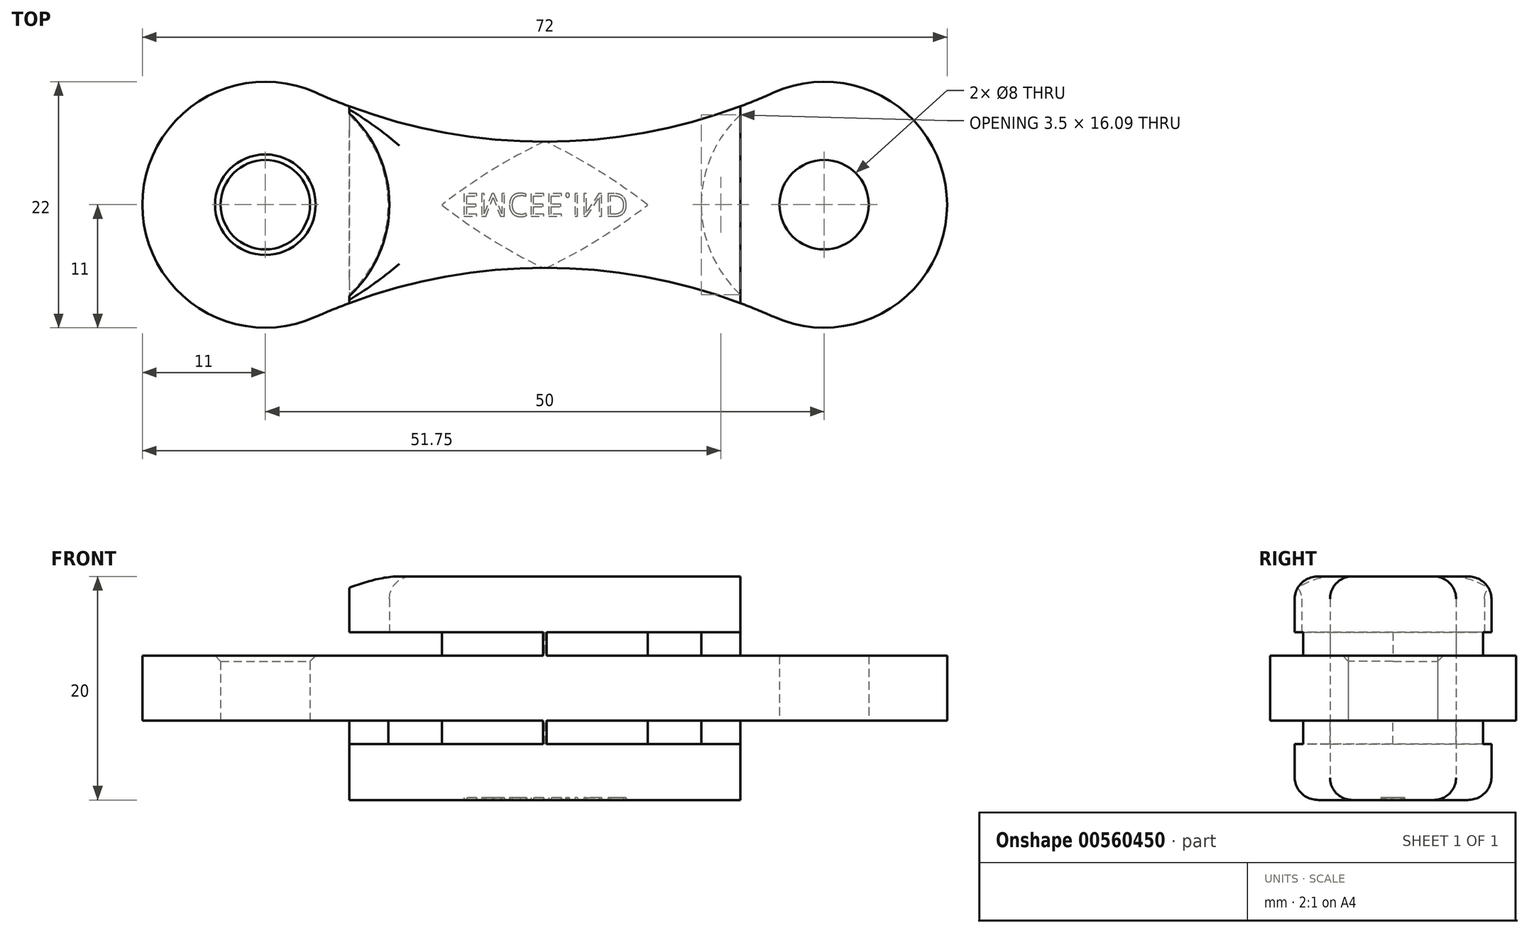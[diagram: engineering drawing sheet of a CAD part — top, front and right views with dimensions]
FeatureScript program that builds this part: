
annotation { "Feature Type Name" : "Feature", "Feature Type Description" : "" }
export const myFeature = defineFeature(function(context is Context, id is Id, definition is map)
    precondition{}
    {
        {
            var Q0;
            Q0=qCreatedBy(makeId("Top.planeOp"),FACE);
            var sketch = newSketch(context, id + "F0", { "sketchPlane" : qUnion([Q0])});
            skArc(sketch, "E0", {"start": v(-20.5, 10.03) * mm, "mid": v(-36, 0) * mm, "end": v(-20.5, -10.03) * mm});
            skArc(sketch, "E1", {"start": v(20.5, -10.03) * mm, "mid": v(36, 0) * mm, "end": v(20.5, 10.03) * mm});
            skArc(sketch, "E2", {"start": v(-20.5, 10.03) * mm, "mid": v(0, 5.64) * mm, "end": v(20.5, 10.03) * mm});
            skLineSegment(sketch, "E3", {"start": v(-25, 0) * mm, "end": v(25, 0) * mm, "construction": true});
            skArc(sketch, "E4.MirrorC", {"start": v(-20.5, -10.03) * mm, "mid": v(0, -5.64) * mm, "end": v(20.5, -10.03) * mm});
            skSolve(sketch);
        }
        {
            var Q0;
            Q0=makeQuery(id+"F0.imprint","IMPRINT",FACE,{"disambiguationData":[TD([[makeQuery(id+"F0.imprint","IMPRINT",EDGE,{"derivedFrom":sQuery(id+"F0.wireOp",EDGE,"E0")}),1.0]])]});
            extrude(context, id + "F1", {"entities" : qUnion([Q0]), "endBound" : BoundingType.SYMMETRIC, "depth" : 20 * mm, "offsetDistance" : 25 * mm});
        }
        {
            var Q0;
            Q0=qCreatedBy(makeId("Front.planeOp"),FACE);
            var sketch = newSketch(context, id + "F2", { "sketchPlane" : qUnion([Q0])});
            skLineSegment(sketch, "E5.bottom", {"start": v(-17.5, -15) * mm, "end": v(-52.5, -15) * mm});
            skLineSegment(sketch, "E5.top", {"start": v(-17.5, -2.9) * mm, "end": v(-52.5, -2.9) * mm});
            skLineSegment(sketch, "E5.left", {"start": v(-17.5, -15) * mm, "end": v(-17.5, -2.9) * mm});
            skLineSegment(sketch, "E5.right", {"start": v(-52.5, -15) * mm, "end": v(-52.5, -2.9) * mm});
            skPoint(sketch, "E5.middle", {"position": v(-35, -8.95) * mm});
            skLineSegment(sketch, "E6", {"start": v(0, 15.36) * mm, "end": v(0, 51.66) * mm, "construction": true});
            skLineSegment(sketch, "E7.MirrorCS", {"start": v(17.5, -15) * mm, "end": v(17.5, -2.9) * mm});
            skLineSegment(sketch, "E8.MirrorCS", {"start": v(17.5, -15) * mm, "end": v(52.5, -15) * mm});
            skLineSegment(sketch, "E9.MirrorCS", {"start": v(17.5, -2.9) * mm, "end": v(52.5, -2.9) * mm});
            skLineSegment(sketch, "E10.MirrorCS", {"start": v(52.5, -15) * mm, "end": v(52.5, -2.9) * mm});
            skLineSegment(sketch, "E11", {"start": v(0, 0) * mm, "end": v(62.43, 0) * mm, "construction": true});
            skLineSegment(sketch, "E12.MirrorCS", {"start": v(-17.5, 2.9) * mm, "end": v(-52.5, 2.9) * mm});
            skLineSegment(sketch, "E13.MirrorCS", {"start": v(-52.5, 15) * mm, "end": v(-52.5, 2.9) * mm});
            skLineSegment(sketch, "E14.MirrorCS", {"start": v(-17.5, 15) * mm, "end": v(-52.5, 15) * mm});
            skLineSegment(sketch, "E15.MirrorCS", {"start": v(-17.5, 15) * mm, "end": v(-17.5, 2.9) * mm});
            skLineSegment(sketch, "E16.MirrorCS", {"start": v(17.5, 15) * mm, "end": v(17.5, 2.9) * mm});
            skLineSegment(sketch, "E17.MirrorCS", {"start": v(17.5, 2.9) * mm, "end": v(52.5, 2.9) * mm});
            skLineSegment(sketch, "E18.MirrorCS", {"start": v(17.5, 15) * mm, "end": v(52.5, 15) * mm});
            skLineSegment(sketch, "E19.MirrorCS", {"start": v(52.5, 15) * mm, "end": v(52.5, 2.9) * mm});
            skSolve(sketch);
        }
        {
            var Q0;
            Q0=makeQuery(id+"F2.imprint","IMPRINT",FACE,{"disambiguationData":[TD([[makeQuery(id+"F2.imprint","IMPRINT",EDGE,{"derivedFrom":sQuery(id+"F2.wireOp",EDGE,"E12.MirrorCS")}),-1.0]])]});
            var Q1;
            Q1=makeQuery(id+"F2.imprint","IMPRINT",FACE,{"disambiguationData":[TD([[makeQuery(id+"F2.imprint","IMPRINT",EDGE,{"derivedFrom":sQuery(id+"F2.wireOp",EDGE,"E5.bottom")}),-1.0]])]});
            var Q2;
            Q2=makeQuery(id+"F2.imprint","IMPRINT",FACE,{"disambiguationData":[TD([[makeQuery(id+"F2.imprint","IMPRINT",EDGE,{"derivedFrom":sQuery(id+"F2.wireOp",EDGE,"E16.MirrorCS")}),1.0]])]});
            var Q3;
            Q3=makeQuery(id+"F2.imprint","IMPRINT",FACE,{"disambiguationData":[TD([[makeQuery(id+"F2.imprint","IMPRINT",EDGE,{"derivedFrom":sQuery(id+"F2.wireOp",EDGE,"E7.MirrorCS")}),-1.0]])]});
            extrude(context, id + "F3", {"entities" : qUnion([Q0, Q1, Q2, Q3]), "operationType" : NewBodyOperationType.REMOVE, "endBound" : BoundingType.SYMMETRIC, "oppositeDirection" : true, "depth" : 25 * mm, "offsetDistance" : 25 * mm});
        }
        {
            var Q0;
            Q0=makeQuery(id+"F3.boolean.opBoolean","COPY",FACE,{"derivedFrom":makeQuery(id+"F3.opExtrude","SWEPT_FACE",FACE,{"disambiguationData":[OSD([sQuery(id+"F2.wireOp",EDGE,"E12.MirrorCS")])]})});
            var sketch = newSketch(context, id + "F4", { "sketchPlane" : qUnion([Q0])});
            skCircle(sketch, "E20", {"center": v(-25, 0) * mm, "radius": 11.1 * mm});
            skLineSegment(sketch, "E21", {"start": v(0, -2.73) * mm, "end": v(0, 23.97) * mm, "construction": true});
            skCircle(sketch, "E22.MirrorC", {"center": v(25, 0) * mm, "radius": 11.1 * mm});
            skLineSegment(sketch, "E23", {"start": v(0, -6.47) * mm, "end": v(-9.77, -6.47) * mm});
            skSolve(sketch);
        }
        {
            var Q0;
            {var subQ0=sQuery(id+"F4.wireOp",EDGE,"E20");var subQ1=makeQuery(id+"F3.boolean.opBoolean","COPY",EDGE,{"derivedFrom":makeQuery(id+"F3.opExtrude","SWEPT_EDGE",EDGE,{"disambiguationData":[OSD([sQuery(id+"F2.wireOp",EDGE,"E12.MirrorCS"),sQuery(id+"F2.wireOp",EDGE,"E15.MirrorCS")])]})});var subQ2=makeQuery(id+"F4.imprint","INTERSECT",VERTEX,{"disambiguationData":[OD(0.0)],"derivedFrom":[subQ1,subQ0]});Q0=makeQuery(id+"F4.imprint","IMPRINT",FACE,{"disambiguationData":[TD([[makeQuery(id+"F4.imprint","IMPRINT",EDGE,{"disambiguationData":[TD([[subQ2,1.0]])],"derivedFrom":subQ0}),1.0]])]});}
            var Q1;
            {var subQ1=sQuery(id+"F2.wireOp",EDGE,"E12.MirrorCS");var subQ5=makeQuery(id+"F3.opExtrude","SWEPT_FACE",FACE,{"disambiguationData":[OSD([subQ1])]});var subQ8=makeQuery(id+"F3.boolean.opBoolean","INTERSECT",EDGE,{"derivedFrom":[makeQuery(id+"F1.opExtrude","SWEPT_FACE",FACE,{"disambiguationData":[OSD([sQuery(id+"F0.wireOp",EDGE,"E0")])]}),subQ5]});Q1=makeQuery(id+"F4.imprint","IMPRINT",FACE,{"disambiguationData":[TD([[makeQuery(id+"F4.imprint","IMPRINT",EDGE,{"derivedFrom":subQ8}),1.0]])]});}
            var Q2;
            Q2=makeQuery(id+"F4.imprint","IMPRINT",FACE,{"disambiguationData":[TD([[makeQuery(id+"F4.imprint","IMPRINT",EDGE,{"derivedFrom":sQuery(id+"F4.wireOp",EDGE,"E22.MirrorC")}),-1.0]])]});
            extrude(context, id + "F5", {"entities" : qUnion([Q0, Q1, Q2]), "operationType" : NewBodyOperationType.REMOVE, "depth" : 10 * mm, "offsetDistance" : 25 * mm});
        }
        {
            var Q0;
            Q0=makeQuery(id+"F3.boolean.opBoolean","COPY",FACE,{"derivedFrom":makeQuery(id+"F3.opExtrude","SWEPT_FACE",FACE,{"disambiguationData":[OSD([sQuery(id+"F2.wireOp",EDGE,"E5.top")])]})});
            var sketch = newSketch(context, id + "F6", { "sketchPlane" : qUnion([Q0])});
            skCircle(sketch, "E24", {"center": v(-25, 0) * mm, "radius": 11.1 * mm});
            skLineSegment(sketch, "E25", {"start": v(0, -7.37) * mm, "end": v(0, 19.33) * mm, "construction": true});
            skCircle(sketch, "E26.MirrorC", {"center": v(25, 0) * mm, "radius": 11.1 * mm});
            skSolve(sketch);
        }
        {
            var Q0;
            Q0=makeQuery(id+"F6.imprint","IMPRINT",FACE,{"disambiguationData":[TD([[makeQuery(id+"F6.imprint","IMPRINT",EDGE,{"derivedFrom":sQuery(id+"F6.wireOp",EDGE,"E26.MirrorC")}),-1.0]])]});
            var Q1;
            {var subQ1=sQuery(id+"F2.wireOp",EDGE,"E5.top");var subQ5=makeQuery(id+"F3.opExtrude","SWEPT_FACE",FACE,{"disambiguationData":[OSD([subQ1])]});var subQ8=makeQuery(id+"F3.boolean.opBoolean","INTERSECT",EDGE,{"derivedFrom":[makeQuery(id+"F1.opExtrude","SWEPT_FACE",FACE,{"disambiguationData":[OSD([sQuery(id+"F0.wireOp",EDGE,"E0")])]}),subQ5]});Q1=makeQuery(id+"F6.imprint","IMPRINT",FACE,{"disambiguationData":[TD([[makeQuery(id+"F6.imprint","IMPRINT",EDGE,{"derivedFrom":subQ8}),-1.0]])]});}
            var Q2;
            {var subQ0=sQuery(id+"F6.wireOp",EDGE,"E24");var subQ1=makeQuery(id+"F3.boolean.opBoolean","COPY",EDGE,{"derivedFrom":makeQuery(id+"F3.opExtrude","SWEPT_EDGE",EDGE,{"disambiguationData":[OSD([sQuery(id+"F2.wireOp",EDGE,"E5.top"),sQuery(id+"F2.wireOp",EDGE,"E5.left")])]})});var subQ2=makeQuery(id+"F6.imprint","INTERSECT",VERTEX,{"disambiguationData":[OD(0.0)],"derivedFrom":[subQ1,subQ0]});Q2=makeQuery(id+"F6.imprint","IMPRINT",FACE,{"disambiguationData":[TD([[makeQuery(id+"F6.imprint","IMPRINT",EDGE,{"disambiguationData":[TD([[subQ2,1.0]])],"derivedFrom":subQ0}),1.0]])]});}
            extrude(context, id + "F7", {"entities" : qUnion([Q0, Q1, Q2]), "operationType" : NewBodyOperationType.REMOVE, "depth" : 10 * mm, "offsetDistance" : 25 * mm});
        }
        {
            var Q0;
            Q0=qCreatedBy(makeId("Front.planeOp"),FACE);
            var sketch = newSketch(context, id + "F8", { "sketchPlane" : qUnion([Q0])});
            skLineSegment(sketch, "E27.bottom", {"start": v(2, 5) * mm, "end": v(-10, 5) * mm});
            skLineSegment(sketch, "E27.top", {"start": v(2, -5) * mm, "end": v(-10, -5) * mm});
            skLineSegment(sketch, "E27.left", {"start": v(5, 2) * mm, "end": v(5, -2) * mm});
            skLineSegment(sketch, "E27.right", {"start": v(-13, 2) * mm, "end": v(-13, -2) * mm});
            skPoint(sketch, "E27.middle", {"position": v(-2, 0) * mm});
            skPoint(sketch, "E28.visualSharp", {"position": v(-13, 5) * mm});
            skArc(sketch, "E28.filletArc", {"start": v(-10, 5) * mm, "mid": v(-12.12, 4.12) * mm, "end": v(-13, 2) * mm});
            skPoint(sketch, "E29.visualSharp", {"position": v(-13, -5) * mm});
            skArc(sketch, "E29.filletArc", {"start": v(-13, -2) * mm, "mid": v(-12.12, -4.12) * mm, "end": v(-10, -5) * mm});
            skPoint(sketch, "E30.visualSharp", {"position": v(5, -5) * mm});
            skArc(sketch, "E30.filletArc", {"start": v(2, -5) * mm, "mid": v(4.12, -4.12) * mm, "end": v(5, -2) * mm});
            skPoint(sketch, "E31.visualSharp", {"position": v(5, 5) * mm});
            skArc(sketch, "E31.filletArc", {"start": v(5, 2) * mm, "mid": v(4.12, 4.12) * mm, "end": v(2, 5) * mm});
            skSolve(sketch);
        }
        {
            var Q0;
            Q0=makeQuery(id+"F7.boolean.opBoolean","INTERSECT",EDGE,{"derivedFrom":[makeQuery(id+"F1.opExtrude","CAP_FACE",FACE,{"disambiguationData":[OSD([sQuery(id+"F0.wireOp",EDGE,"E0"),sQuery(id+"F0.wireOp",EDGE,"E1"),sQuery(id+"F0.wireOp",EDGE,"E2"),sQuery(id+"F0.wireOp",EDGE,"E4.MirrorC")])],"isStart":true}),makeQuery(id+"F7.opExtrude","SWEPT_FACE",FACE,{"disambiguationData":[OSD([sQuery(id+"F6.wireOp",EDGE,"E24")])]})]});
            var Q1;
            Q1=makeQuery(id+"F7.boolean.opBoolean","INTERSECT",EDGE,{"derivedFrom":[makeQuery(id+"F1.opExtrude","CAP_FACE",FACE,{"disambiguationData":[OSD([sQuery(id+"F0.wireOp",EDGE,"E0"),sQuery(id+"F0.wireOp",EDGE,"E1"),sQuery(id+"F0.wireOp",EDGE,"E2"),sQuery(id+"F0.wireOp",EDGE,"E4.MirrorC")])],"isStart":true}),makeQuery(id+"F7.opExtrude","SWEPT_FACE",FACE,{"disambiguationData":[OSD([sQuery(id+"F6.wireOp",EDGE,"E26.MirrorC")])]})]});
            var Q2;
            Q2=makeQuery(id+"F1.opExtrude","CAP_EDGE",EDGE,{"disambiguationData":[OSD([sQuery(id+"F0.wireOp",EDGE,"E2")])],"isStart":true});
            var Q3;
            Q3=makeQuery(id+"F1.opExtrude","CAP_EDGE",EDGE,{"disambiguationData":[OSD([sQuery(id+"F0.wireOp",EDGE,"E4.MirrorC")])],"isStart":true});
            var Q4;
            Q4=makeQuery(id+"F5.boolean.opBoolean","INTERSECT",EDGE,{"derivedFrom":[makeQuery(id+"F1.opExtrude","CAP_FACE",FACE,{"disambiguationData":[OSD([sQuery(id+"F0.wireOp",EDGE,"E0"),sQuery(id+"F0.wireOp",EDGE,"E1"),sQuery(id+"F0.wireOp",EDGE,"E2"),sQuery(id+"F0.wireOp",EDGE,"E4.MirrorC")])],"isStart":false}),makeQuery(id+"F5.opExtrude","SWEPT_FACE",FACE,{"disambiguationData":[OSD([sQuery(id+"F4.wireOp",EDGE,"E20")])]})]});
            var Q5;
            Q5=makeQuery(id+"F5.boolean.opBoolean","INTERSECT",EDGE,{"derivedFrom":[makeQuery(id+"F1.opExtrude","CAP_FACE",FACE,{"disambiguationData":[OSD([sQuery(id+"F0.wireOp",EDGE,"E0"),sQuery(id+"F0.wireOp",EDGE,"E1"),sQuery(id+"F0.wireOp",EDGE,"E2"),sQuery(id+"F0.wireOp",EDGE,"E4.MirrorC")])],"isStart":false}),makeQuery(id+"F5.opExtrude","SWEPT_FACE",FACE,{"disambiguationData":[OSD([sQuery(id+"F4.wireOp",EDGE,"E22.MirrorC")])]})]});
            var Q6;
            Q6=makeQuery(id+"F1.opExtrude","CAP_EDGE",EDGE,{"disambiguationData":[OSD([sQuery(id+"F0.wireOp",EDGE,"E2")])],"isStart":false});
            var Q7;
            Q7=makeQuery(id+"F1.opExtrude","CAP_EDGE",EDGE,{"disambiguationData":[OSD([sQuery(id+"F0.wireOp",EDGE,"E4.MirrorC")])],"isStart":false});
            fillet(context, id + "F9", {"entities" : qUnion([Q0, Q1, Q2, Q3, Q4, Q5, Q6, Q7]), "radius" : 2 * mm, "tangentPropagation" : true, "allowEdgeOverflow" : false});
        }
        {
            var Q0;
            {var subQ1=sQuery(id+"F2.wireOp",EDGE,"E5.top");var subQ5=makeQuery(id+"F3.opExtrude","SWEPT_FACE",FACE,{"disambiguationData":[OSD([subQ1])]});var subQ8=makeQuery(id+"F3.boolean.opBoolean","INTERSECT",EDGE,{"derivedFrom":[makeQuery(id+"F1.opExtrude","SWEPT_FACE",FACE,{"disambiguationData":[OSD([sQuery(id+"F0.wireOp",EDGE,"E0")])]}),subQ5]});Q0=makeQuery(id+"F6.imprint","IMPRINT",FACE,{"disambiguationData":[TD([[makeQuery(id+"F6.imprint","IMPRINT",EDGE,{"derivedFrom":subQ8}),-1.0]])]});}
            var sketch = newSketch(context, id + "F10", { "sketchPlane" : qUnion([Q0])});
            skCircle(sketch, "E32", {"center": v(-25, 0) * mm, "radius": 4 * mm});
            skCircle(sketch, "E33", {"center": v(25, 0) * mm, "radius": 4 * mm});
            skSolve(sketch);
        }
        {
            var Q0;
            Q0 = qSketchRegion(id + "F10", true);
            extrude(context, id + "F11", {"entities" : qUnion([Q0]), "operationType" : NewBodyOperationType.REMOVE, "endBound" : BoundingType.THROUGH_ALL, "oppositeDirection" : true, "depth" : 25 * mm, "offsetDistance" : 25 * mm});
        }
        {
            var Q0;
            {var subQ0=sQuery(id+"F2.wireOp",EDGE,"E12.MirrorCS");Q0=makeQuery(id+"F5.boolean.opBoolean","MERGE",FACE,{"derivedFrom":[makeQuery(id+"F3.boolean.opBoolean","COPY",FACE,{"derivedFrom":makeQuery(id+"F3.opExtrude","SWEPT_FACE",FACE,{"disambiguationData":[OSD([subQ0])]})}),makeQuery(id+"F5.opExtrude","CAP_FACE",FACE,{"disambiguationData":[OSD([sQuery(id+"F0.wireOp",EDGE,"E0"),sQuery(id+"F0.wireOp",EDGE,"E2"),sQuery(id+"F0.wireOp",EDGE,"E4.MirrorC"),subQ0,sQuery(id+"F4.wireOp",EDGE,"E20")])],"isStart":true})]});}
            var sketch = newSketch(context, id + "F12", { "sketchPlane" : qUnion([Q0])});
            skArc(sketch, "E34", {"start": v(-13.16, 16.12) * mm, "mid": v(-45, 0) * mm, "end": v(-13.16, -16.12) * mm});
            skLineSegment(sketch, "E35", {"start": v(0, -6.46) * mm, "end": v(-13.16, -16.12) * mm});
            skLineSegment(sketch, "E36", {"start": v(0, 6.46) * mm, "end": v(-13.16, 16.12) * mm});
            skLineSegment(sketch, "E37.MirrorCS", {"start": v(0, -6.46) * mm, "end": v(13.16, -16.12) * mm});
            skLineSegment(sketch, "E38.MirrorCS", {"start": v(0, 6.46) * mm, "end": v(13.16, 16.12) * mm});
            skArc(sketch, "E39.MirrorCS", {"start": v(13.16, 16.12) * mm, "mid": v(45, 0) * mm, "end": v(13.16, -16.12) * mm});
            skArc(sketch, "E40", {"start": v(-9.2, -0.01) * mm, "mid": v(-4.76, -3.12) * mm, "end": v(0, -5.72) * mm});
            skArc(sketch, "E41", {"start": v(9.2, -0.01) * mm, "mid": v(4.76, 3.08) * mm, "end": v(0, 5.67) * mm});
            skLineSegment(sketch, "E42", {"start": v(0, 0) * mm, "end": v(0, -2.6) * mm, "construction": true});
            skArc(sketch, "E43.MirrorCS", {"start": v(-9.2, -0.01) * mm, "mid": v(-4.76, 3.08) * mm, "end": v(0, 5.67) * mm});
            skArc(sketch, "E44.MirrorCS", {"start": v(9.2, -0.01) * mm, "mid": v(4.76, -3.12) * mm, "end": v(0, -5.72) * mm});
            skPoint(sketch, "E45.orphan", {"position": v(-19.29, -10.56) * mm});
            skPoint(sketch, "E46.orphan", {"position": v(-19.22, 10.49) * mm});
            skPoint(sketch, "E47.orphan", {"position": v(19.22, 10.49) * mm});
            skPoint(sketch, "E48.orphan", {"position": v(19.29, -10.56) * mm});
            skCircle(sketch, "E49", {"center": v(-25, 0) * mm, "radius": 11 * mm});
            skCircle(sketch, "E50", {"center": v(25, 0) * mm, "radius": 11 * mm});
            skSolve(sketch);
        }
        {
            var Q0;
            Q0=makeQuery(id+"F7.boolean.opBoolean","MERGE",FACE,{"derivedFrom":[makeQuery(id+"F3.boolean.opBoolean","COPY",FACE,{"derivedFrom":makeQuery(id+"F3.opExtrude","SWEPT_FACE",FACE,{"disambiguationData":[OSD([sQuery(id+"F2.wireOp",EDGE,"E9.MirrorCS")])]})}),makeQuery(id+"F7.opExtrude","CAP_FACE",FACE,{"disambiguationData":[OSD([sQuery(id+"F6.wireOp",EDGE,"E26.MirrorC")])],"isStart":true})]});
            var sketch = newSketch(context, id + "F13", { "sketchPlane" : qUnion([Q0])});
            skArc(sketch, "E51", {"start": v(-13.16, 16.12) * mm, "mid": v(-45, 0) * mm, "end": v(-13.16, -16.12) * mm});
            skLineSegment(sketch, "E52", {"start": v(0, -6.46) * mm, "end": v(-13.16, -16.12) * mm});
            skLineSegment(sketch, "E53", {"start": v(0, 6.46) * mm, "end": v(-13.16, 16.12) * mm});
            skLineSegment(sketch, "E54.MirrorCS", {"start": v(0, -6.46) * mm, "end": v(13.16, -16.12) * mm});
            skLineSegment(sketch, "E55.MirrorCS", {"start": v(0, 6.46) * mm, "end": v(13.16, 16.12) * mm});
            skArc(sketch, "E56.MirrorCS", {"start": v(13.16, 16.12) * mm, "mid": v(45, 0) * mm, "end": v(13.16, -16.12) * mm});
            skArc(sketch, "E57", {"start": v(0, -5.67) * mm, "mid": v(4.76, -3.08) * mm, "end": v(9.2, 0.01) * mm});
            skArc(sketch, "E58", {"start": v(0, 5.72) * mm, "mid": v(-4.76, 3.12) * mm, "end": v(-9.2, 0.01) * mm});
            skLineSegment(sketch, "E59", {"start": v(0, 0) * mm, "end": v(0, 3.2) * mm, "construction": true});
            skArc(sketch, "E60.MirrorCS", {"start": v(0, 5.72) * mm, "mid": v(4.76, 3.12) * mm, "end": v(9.2, 0.01) * mm});
            skArc(sketch, "E61.MirrorCS", {"start": v(0, -5.67) * mm, "mid": v(-4.76, -3.08) * mm, "end": v(-9.2, 0.01) * mm});
            skPoint(sketch, "E62.orphan", {"position": v(-19.29, 10.56) * mm});
            skPoint(sketch, "E63.orphan", {"position": v(19.29, 10.56) * mm});
            skPoint(sketch, "E64.orphan", {"position": v(19.22, -10.49) * mm});
            skPoint(sketch, "E65.orphan", {"position": v(-19.22, -10.49) * mm});
            skCircle(sketch, "E66", {"center": v(-25, 0) * mm, "radius": 11 * mm});
            skCircle(sketch, "E67", {"center": v(25, 0) * mm, "radius": 11 * mm});
            skSolve(sketch);
        }
        {
            var Q0;
            Q0=makeQuery(id+"F13.imprint","IMPRINT",FACE,{"disambiguationData":[TD([[makeQuery(id+"F13.imprint","IMPRINT",EDGE,{"derivedFrom":sQuery(id+"F13.wireOp",EDGE,"E51")}),1.0]])]});
            var Q1;
            Q1=makeQuery(id+"F13.imprint","IMPRINT",FACE,{"disambiguationData":[TD([[makeQuery(id+"F13.imprint","IMPRINT",EDGE,{"derivedFrom":sQuery(id+"F13.wireOp",EDGE,"E54.MirrorCS")}),1.0]])]});
            extrude(context, id + "F14", {"entities" : qUnion([Q0, Q1]), "operationType" : NewBodyOperationType.REMOVE, "depth" : 2.1 * mm, "offsetDistance" : 25 * mm});
        }
        {
            var Q0;
            Q0=makeQuery(id+"F12.imprint","IMPRINT",FACE,{"disambiguationData":[TD([[makeQuery(id+"F12.imprint","IMPRINT",EDGE,{"derivedFrom":sQuery(id+"F12.wireOp",EDGE,"E37.MirrorCS")}),1.0]])]});
            var Q1;
            Q1=makeQuery(id+"F12.imprint","IMPRINT",FACE,{"disambiguationData":[TD([[makeQuery(id+"F12.imprint","IMPRINT",EDGE,{"derivedFrom":sQuery(id+"F12.wireOp",EDGE,"E34")}),1.0]])]});
            extrude(context, id + "F15", {"entities" : qUnion([Q0, Q1]), "operationType" : NewBodyOperationType.REMOVE, "depth" : 2.1 * mm, "offsetDistance" : 25 * mm});
        }
        {
            var Q0;
            Q0=makeQuery(id+"F11.boolean.opBoolean","COPY",EDGE,{"derivedFrom":makeQuery(id+"F11.opExtrude","CAP_EDGE",EDGE,{"disambiguationData":[OSD([sQuery(id+"F10.wireOp",EDGE,"E33")])],"isStart":true})});
            var Q1;
            Q1=makeQuery(id+"F11.boolean.opBoolean","COPY",EDGE,{"derivedFrom":makeQuery(id+"F11.opExtrude","CAP_EDGE",EDGE,{"disambiguationData":[OSD([sQuery(id+"F10.wireOp",EDGE,"E32")])],"isStart":true})});
            var Q2;
            Q2=makeQuery(id+"F11.boolean.opBoolean","INTERSECT",EDGE,{"derivedFrom":[makeQuery(id+"F5.boolean.opBoolean","MERGE",FACE,{"derivedFrom":[makeQuery(id+"F3.boolean.opBoolean","COPY",FACE,{"derivedFrom":makeQuery(id+"F3.opExtrude","SWEPT_FACE",FACE,{"disambiguationData":[OSD([sQuery(id+"F2.wireOp",EDGE,"E17.MirrorCS")])]})}),makeQuery(id+"F5.opExtrude","CAP_FACE",FACE,{"disambiguationData":[OSD([sQuery(id+"F4.wireOp",EDGE,"E22.MirrorC")])],"isStart":true})]}),makeQuery(id+"F11.opExtrude","SWEPT_FACE",FACE,{"disambiguationData":[OSD([sQuery(id+"F10.wireOp",EDGE,"E33")])]})]});
            var Q3;
            {var subQ0=sQuery(id+"F2.wireOp",EDGE,"E12.MirrorCS");Q3=makeQuery(id+"F11.boolean.opBoolean","INTERSECT",EDGE,{"derivedFrom":[makeQuery(id+"F5.boolean.opBoolean","MERGE",FACE,{"derivedFrom":[makeQuery(id+"F3.boolean.opBoolean","COPY",FACE,{"derivedFrom":makeQuery(id+"F3.opExtrude","SWEPT_FACE",FACE,{"disambiguationData":[OSD([subQ0])]})}),makeQuery(id+"F5.opExtrude","CAP_FACE",FACE,{"disambiguationData":[OSD([sQuery(id+"F0.wireOp",EDGE,"E0"),sQuery(id+"F0.wireOp",EDGE,"E2"),sQuery(id+"F0.wireOp",EDGE,"E4.MirrorC"),subQ0,sQuery(id+"F4.wireOp",EDGE,"E20")])],"isStart":true})]}),makeQuery(id+"F11.opExtrude","SWEPT_FACE",FACE,{"disambiguationData":[OSD([sQuery(id+"F10.wireOp",EDGE,"E32")])]})]});}
            chamfer(context, id + "F16", {"entities" : qUnion([Q0, Q1, Q2, Q3]), "width" : .5 * mm, "tangentPropagation" : true});
        }
        {
            var Q0;
            Q0=makeQuery(id+"F1.opExtrude","CAP_FACE",FACE,{"disambiguationData":[OSD([sQuery(id+"F0.wireOp",EDGE,"E0"),sQuery(id+"F0.wireOp",EDGE,"E1"),sQuery(id+"F0.wireOp",EDGE,"E2"),sQuery(id+"F0.wireOp",EDGE,"E4.MirrorC")])],"isStart":true});
            var sketch = newSketch(context, id + "F17", { "sketchPlane" : qUnion([Q0])});
            skText(sketch, "E68", { "text": "EMCEE.IND", "fontName": "OpenSans-Regular.ttf"});
            const initialGuessF17  = {"E68": [-0.0075, -0.001, 1, 0, 0.00206]};
            skSetInitialGuess(sketch, initialGuessF17);
            skSolve(sketch);
        }
        {
            var Q0;
            Q0 = qSketchRegion(id + "F17", true);
            extrude(context, id + "F18", {"entities" : qUnion([Q0]), "operationType" : NewBodyOperationType.REMOVE, "oppositeDirection" : true, "depth" : 0.2 * mm, "offsetDistance" : 25 * mm});
        }
    });
